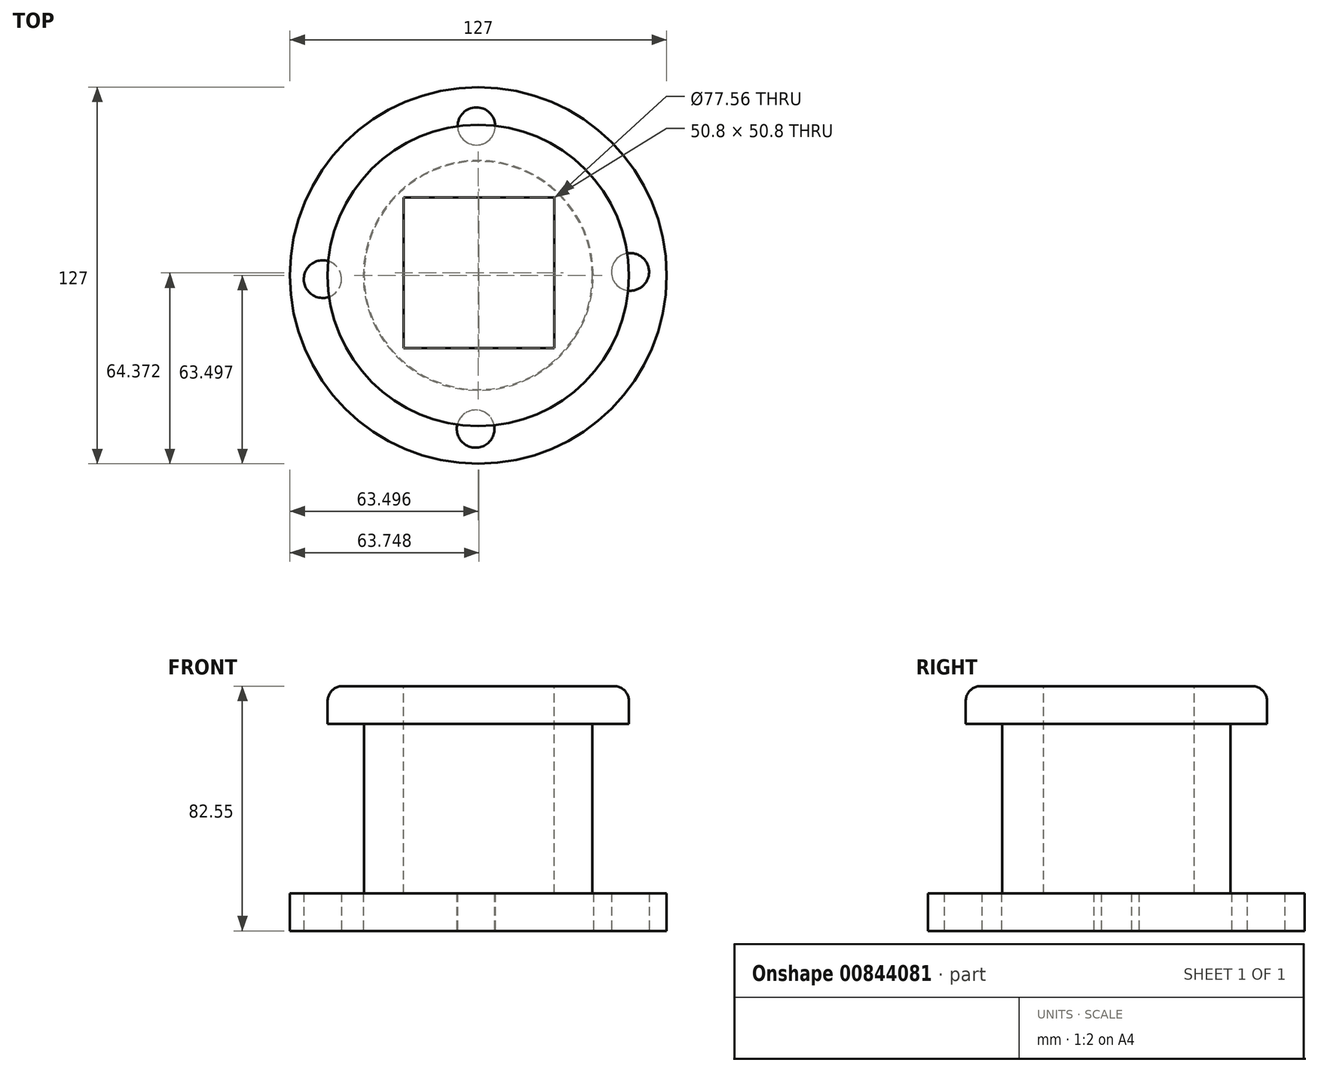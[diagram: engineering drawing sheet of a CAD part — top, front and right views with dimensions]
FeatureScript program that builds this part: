
annotation { "Feature Type Name" : "Feature", "Feature Type Description" : "" }
export const myFeature = defineFeature(function(context is Context, id is Id, definition is map)
    precondition{}
    {
        {
            var Q0;
            Q0=qCreatedBy(makeId("Top.planeOp"),FACE);
            var sketch = newSketch(context, id + "F0", { "sketchPlane" : qUnion([Q0])});
            skCircle(sketch, "E0", {"center": v(9.15, 16.2) * mm, "radius": 63.5 * mm});
            skLineSegment(sketch, "E1.bottom", {"start": v(-16.59, 42) * mm, "end": v(34.21, 42) * mm});
            skLineSegment(sketch, "E1.top", {"start": v(-16.59, -8.8) * mm, "end": v(34.21, -8.8) * mm});
            skLineSegment(sketch, "E1.left", {"start": v(-16.59, 42) * mm, "end": v(-16.59, -8.8) * mm});
            skLineSegment(sketch, "E1.right", {"start": v(34.21, 42) * mm, "end": v(34.21, -8.8) * mm});
            skCircle(sketch, "E2", {"center": v(8.53, 66.54) * mm, "radius": 6.35 * mm});
            skCircle(sketch, "E3", {"center": v(-43.32, 14.96) * mm, "radius": 6.35 * mm});
            skCircle(sketch, "E4", {"center": v(8.26, -35.54) * mm, "radius": 6.35 * mm});
            skCircle(sketch, "E5", {"center": v(9.15, 16.2) * mm, "radius": 38.78 * mm});
            skCircle(sketch, "E6", {"center": v(60.38, 17.39) * mm, "radius": 6.35 * mm});
            skSolve(sketch);
        }
        {
            var Q0;
            Q0 = qSketchRegion(id + "F0", true);
            extrude(context, id + "F1", {"entities" : qUnion([Q0]), "depth" : 12.7 * mm, "offsetDistance" : 25.4 * mm});
        }
        {
            var Q0;
            Q0=makeQuery(id+"F1.opExtrude","CAP_FACE",FACE,{"disambiguationData":[OSD([sQuery(id+"F0.wireOp",EDGE,"E0"),sQuery(id+"F0.wireOp",EDGE,"E2"),sQuery(id+"F0.wireOp",EDGE,"E3"),sQuery(id+"F0.wireOp",EDGE,"E4"),sQuery(id+"F0.wireOp",EDGE,"E5"),sQuery(id+"F0.wireOp",EDGE,"E6")])],"isStart":false});
            var sketch = newSketch(context, id + "F2", { "sketchPlane" : qUnion([Q0])});
            skCircle(sketch, "E7", {"center": v(9.15, 16.2) * mm, "radius": 38.5 * mm});
            skSolve(sketch);
        }
        {
            var Q0;
            Q0 = qSketchRegion(id + "F2", true);
            extrude(context, id + "F3", {"entities" : qUnion([Q0]), "depth" : 57.15 * mm, "offsetDistance" : 25.4 * mm});
        }
        {
            var Q0;
            Q0=makeQuery(id+"F3.opExtrude","CAP_FACE",FACE,{"disambiguationData":[OSD([sQuery(id+"F2.wireOp",EDGE,"E7")])],"isStart":false});
            var sketch = newSketch(context, id + "F4", { "sketchPlane" : qUnion([Q0])});
            skCircle(sketch, "E8", {"center": v(9.15, 16.2) * mm, "radius": 50.8 * mm});
            skSolve(sketch);
        }
        {
            var Q0;
            Q0=makeQuery(id+"F4.imprint","IMPRINT",FACE,{"disambiguationData":[TD([[makeQuery(id+"F4.imprint","IMPRINT",EDGE,{"derivedFrom":sQuery(id+"F4.wireOp",EDGE,"E8")}),1.0]])]});
            var Q1;
            Q1=makeQuery(id+"F4.imprint","IMPRINT",FACE,{"disambiguationData":[TD([[makeQuery(id+"F4.imprint","IMPRINT",EDGE,{"derivedFrom":makeQuery(id+"F3.opExtrude","CAP_EDGE",EDGE,{"disambiguationData":[OSD([sQuery(id+"F2.wireOp",EDGE,"E7")])],"isStart":false})}),1.0]])]});
            extrude(context, id + "F5", {"entities" : qUnion([Q0, Q1]), "operationType" : NewBodyOperationType.ADD, "depth" : 12.7 * mm, "offsetDistance" : 25.4 * mm});
        }
        {
            var Q0;
            Q0=makeQuery(id+"F5.opExtrude","CAP_FACE",FACE,{"disambiguationData":[OSD([sQuery(id+"F4.wireOp",EDGE,"E8")])],"isStart":false});
            var sketch = newSketch(context, id + "F6", { "sketchPlane" : qUnion([Q0])});
            skLineSegment(sketch, "E9.bottom", {"start": v(34.8, -8.33) * mm, "end": v(-16, -8.33) * mm});
            skLineSegment(sketch, "E9.top", {"start": v(34.8, 42.47) * mm, "end": v(-16, 42.47) * mm});
            skLineSegment(sketch, "E9.left", {"start": v(34.8, -8.33) * mm, "end": v(34.8, 42.47) * mm});
            skLineSegment(sketch, "E9.right", {"start": v(-16, -8.33) * mm, "end": v(-16, 42.47) * mm});
            skSolve(sketch);
        }
        {
            var Q0;
            Q0=makeQuery(id+"F6.imprint","IMPRINT",FACE,{"disambiguationData":[TD([[makeQuery(id+"F6.imprint","IMPRINT",EDGE,{"derivedFrom":sQuery(id+"F6.wireOp",EDGE,"E9.bottom")}),-1.0]])]});
            extrude(context, id + "F7", {"entities" : qUnion([Q0]), "operationType" : NewBodyOperationType.REMOVE, "oppositeDirection" : true, "depth" : 111 * mm, "offsetDistance" : 25.4 * mm});
        }
        {
            var Q0;
            Q0=makeQuery(id+"F5.opExtrude","CAP_EDGE",EDGE,{"disambiguationData":[OSD([sQuery(id+"F4.wireOp",EDGE,"E8")])],"isStart":false});
            fillet(context, id + "F8", {"entities" : qUnion([Q0]), "radius" : 5.08 * mm, "tangentPropagation" : true, "allowEdgeOverflow" : false});
        }
    });
